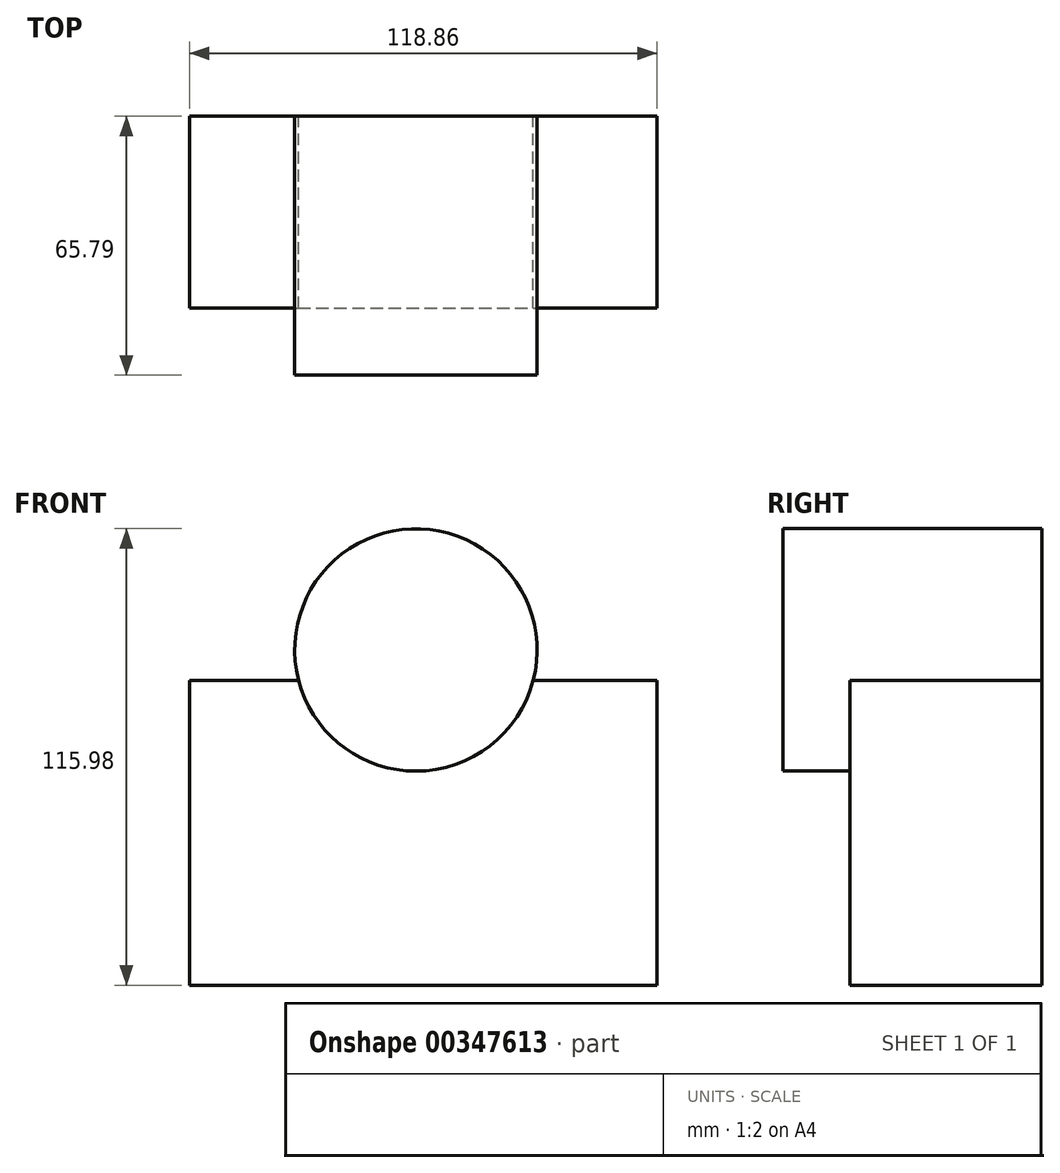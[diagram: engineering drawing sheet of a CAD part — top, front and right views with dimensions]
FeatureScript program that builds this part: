
annotation { "Feature Type Name" : "Feature", "Feature Type Description" : "" }
export const myFeature = defineFeature(function(context is Context, id is Id, definition is map)
    precondition{}
    {
        {
            var Q0;
            Q0=qCreatedBy(makeId("Front.planeOp"),FACE);
            var sketch = newSketch(context, id + "F0", { "sketchPlane" : qUnion([Q0])});
            skLineSegment(sketch, "E0.bottom", {"start": v(-57.56, 38.57) * mm, "end": v(61.3, 38.57) * mm});
            skLineSegment(sketch, "E0.top", {"start": v(-57.56, -38.85) * mm, "end": v(61.3, -38.85) * mm});
            skLineSegment(sketch, "E0.left", {"start": v(-57.56, 38.57) * mm, "end": v(-57.56, -38.85) * mm});
            skLineSegment(sketch, "E0.right", {"start": v(61.3, 38.57) * mm, "end": v(61.3, -38.85) * mm});
            skSolve(sketch);
        }
        {
            var Q0;
            Q0=makeQuery(id+"F0.imprint","IMPRINT",FACE,{"disambiguationData":[TD([[makeQuery(id+"F0.imprint","IMPRINT",EDGE,{"derivedFrom":sQuery(id+"F0.wireOp",EDGE,"E0.bottom")}),-1.0]])]});
            extrude(context, id + "F1", {"entities" : qUnion([Q0]), "depth" : 48.77 * mm});
        }
        {
            var Q0;
            Q0=qCreatedBy(makeId("Front.planeOp"),FACE);
            var sketch = newSketch(context, id + "F2", { "sketchPlane" : qUnion([Q0])});
            skCircle(sketch, "E1", {"center": v(-38, 15.9) * mm, "radius": 19.23 * mm});
            skCircle(sketch, "E2", {"center": v(0, -12.6) * mm, "radius": 18.96 * mm});
            skCircle(sketch, "E3", {"center": v(15.4, -21.9) * mm, "radius": 29.88 * mm});
            skSolve(sketch);
        }
        {
            var Q0;
            Q0=sQuery(id+"F2.wireOp",EDGE,"E2");
            extrude(context, id + "F3", {"bodyType" : ToolBodyType.SURFACE, "surfaceEntities" : qUnion([Q0]), "depth" : 73.9 * mm});
        }
        {
            var Q0;
            Q0=qCreatedBy(makeId("Front.planeOp"),FACE);
            var sketch = newSketch(context, id + "F4", { "sketchPlane" : qUnion([Q0])});
            skCircle(sketch, "E4", {"center": v(0, 46.34) * mm, "radius": 30.8 * mm});
            skSolve(sketch);
        }
        {
            var Q0;
            Q0=makeQuery(id+"F4.imprint","IMPRINT",FACE,{"disambiguationData":[TD([[makeQuery(id+"F4.imprint","IMPRINT",EDGE,{"derivedFrom":sQuery(id+"F4.wireOp",EDGE,"E4")}),1.0]])]});
            extrude(context, id + "F5", {"entities" : qUnion([Q0]), "operationType" : NewBodyOperationType.ADD, "depth" : 65.8 * mm});
        }
    });
